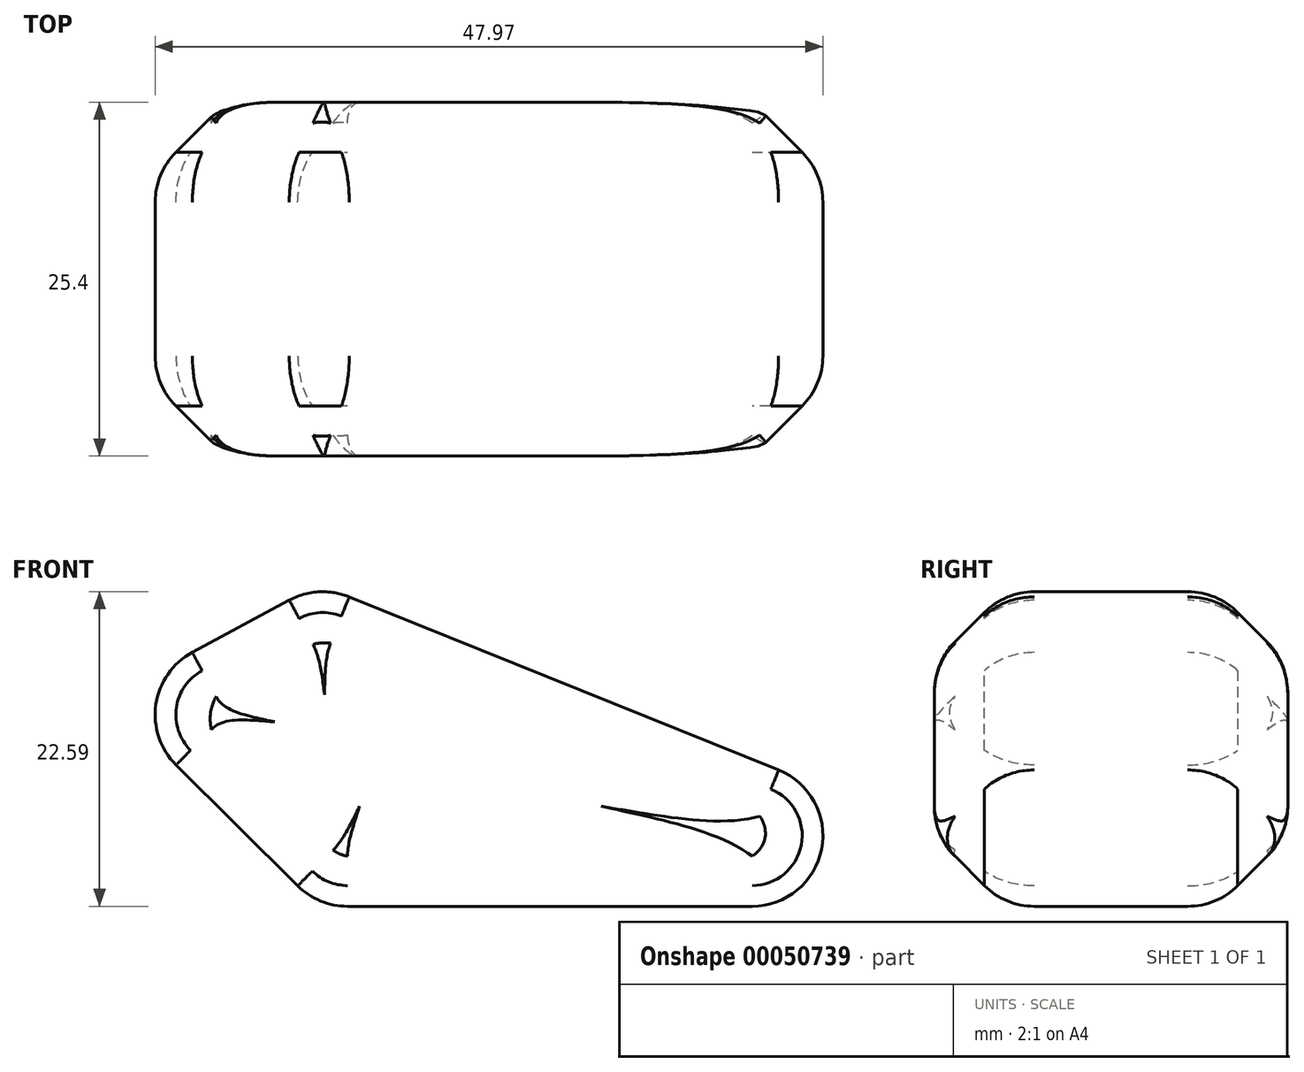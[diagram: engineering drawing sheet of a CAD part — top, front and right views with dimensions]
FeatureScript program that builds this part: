
annotation { "Feature Type Name" : "Feature", "Feature Type Description" : "" }
export const myFeature = defineFeature(function(context is Context, id is Id, definition is map)
    precondition{}
    {
        {
            var Q0;
            Q0=qCreatedBy(makeId("Front.planeOp"),FACE);
            var sketch = newSketch(context, id + "F0", { "sketchPlane" : qUnion([Q0])});
            skLineSegment(sketch, "E0", {"start": v(0, 0) * mm, "end": v(-15.1, 14.98) * mm});
            skLineSegment(sketch, "E1", {"start": v(-15.1, 14.98) * mm, "end": v(0, 23.1) * mm});
            skLineSegment(sketch, "E2", {"start": v(0, 23.1) * mm, "end": v(57.37, 0) * mm});
            skLineSegment(sketch, "E3", {"start": v(0, 0) * mm, "end": v(57.37, 0) * mm});
            skSolve(sketch);
        }
        {
            var Q0;
            Q0 = qSketchRegion(id + "F0", true);
            extrude(context, id + "F1", {"entities" : qUnion([Q0]), "depth" : 25.4 * mm});
        }
        {
            var Q0;
            Q0=makeQuery(id+"F1.opExtrude","SWEPT_EDGE",EDGE,{"disambiguationData":[OSD([sQuery(id+"F0.wireOp",EDGE,"E2"),sQuery(id+"F0.wireOp",EDGE,"E3")])]});
            fillet(context, id + "F2", {"entities" : qUnion([Q0]), "radius" : 5.08 * mm, "tangentPropagation" : true, "allowEdgeOverflow" : false});
        }
        {
            var Q0;
            Q0=makeQuery(id+"F1.opExtrude","SWEPT_EDGE",EDGE,{"disambiguationData":[OSD([sQuery(id+"F0.wireOp",EDGE,"E1"),sQuery(id+"F0.wireOp",EDGE,"E2")])]});
            var Q1;
            Q1=makeQuery(id+"F1.opExtrude","SWEPT_EDGE",EDGE,{"disambiguationData":[OSD([sQuery(id+"F0.wireOp",EDGE,"E0"),sQuery(id+"F0.wireOp",EDGE,"E1")])]});
            var Q2;
            Q2=makeQuery(id+"F1.opExtrude","SWEPT_EDGE",EDGE,{"disambiguationData":[OSD([sQuery(id+"F0.wireOp",EDGE,"E0"),sQuery(id+"F0.wireOp",EDGE,"E3")])]});
            fillet(context, id + "F3", {"entities" : qUnion([Q0, Q1, Q2]), "radius" : 5.08 * mm, "tangentPropagation" : true, "allowEdgeOverflow" : false});
        }
        {
            var Q0;
            Q0=makeQuery(id+"F1.opExtrude","CAP_FACE",FACE,{"disambiguationData":[OSD([sQuery(id+"F0.wireOp",EDGE,"E0"),sQuery(id+"F0.wireOp",EDGE,"E1"),sQuery(id+"F0.wireOp",EDGE,"E2"),sQuery(id+"F0.wireOp",EDGE,"E3")])],"isStart":false});
            var Q1;
            Q1=makeQuery(id+"F1.opExtrude","CAP_FACE",FACE,{"disambiguationData":[OSD([sQuery(id+"F0.wireOp",EDGE,"E0"),sQuery(id+"F0.wireOp",EDGE,"E1"),sQuery(id+"F0.wireOp",EDGE,"E2"),sQuery(id+"F0.wireOp",EDGE,"E3")])],"isStart":true});
            chamfer(context, id + "F4", {"entities" : qUnion([Q0, Q1]), "width" : 5.08 * mm, "tangentPropagation" : true});
        }
        {
            var Q0;
            {var subQ0=sQuery(id+"F0.wireOp",EDGE,"E2");Q0=makeQuery(id+"F4.opChamfer","BLEND_EDGE",EDGE,{"blendedFrom":[makeQuery(id+"F1.opExtrude","CAP_EDGE",EDGE,{"disambiguationData":[OSD([subQ0])],"isStart":false}),makeQuery(id+"F1.opExtrude","SWEPT_FACE",FACE,{"disambiguationData":[OSD([subQ0])]})],"blendedInto":[makeQuery(id+"F1.opExtrude","SWEPT_FACE",FACE,{"disambiguationData":[OSD([subQ0])]})]});}
            var Q1;
            {var subQ0=sQuery(id+"F0.wireOp",EDGE,"E2");Q1=makeQuery(id+"F4.opChamfer","BLEND_EDGE",EDGE,{"blendedFrom":[makeQuery(id+"F1.opExtrude","CAP_EDGE",EDGE,{"disambiguationData":[OSD([subQ0])],"isStart":true}),makeQuery(id+"F1.opExtrude","SWEPT_FACE",FACE,{"disambiguationData":[OSD([subQ0])]})],"blendedInto":[makeQuery(id+"F1.opExtrude","SWEPT_FACE",FACE,{"disambiguationData":[OSD([subQ0])]})]});}
            var Q2;
            Q2=makeQuery(id+"F1.opExtrude","CAP_FACE",FACE,{"disambiguationData":[OSD([sQuery(id+"F0.wireOp",EDGE,"E0"),sQuery(id+"F0.wireOp",EDGE,"E1"),sQuery(id+"F0.wireOp",EDGE,"E2"),sQuery(id+"F0.wireOp",EDGE,"E3")])],"isStart":false});
            var Q3;
            Q3=makeQuery(id+"F1.opExtrude","CAP_FACE",FACE,{"disambiguationData":[OSD([sQuery(id+"F0.wireOp",EDGE,"E0"),sQuery(id+"F0.wireOp",EDGE,"E1"),sQuery(id+"F0.wireOp",EDGE,"E2"),sQuery(id+"F0.wireOp",EDGE,"E3")])],"isStart":true});
            fillet(context, id + "F5", {"entities" : qUnion([Q0, Q1, Q2, Q3]), "radius" : 5.08 * mm, "tangentPropagation" : true, "allowEdgeOverflow" : false});
        }
    });
